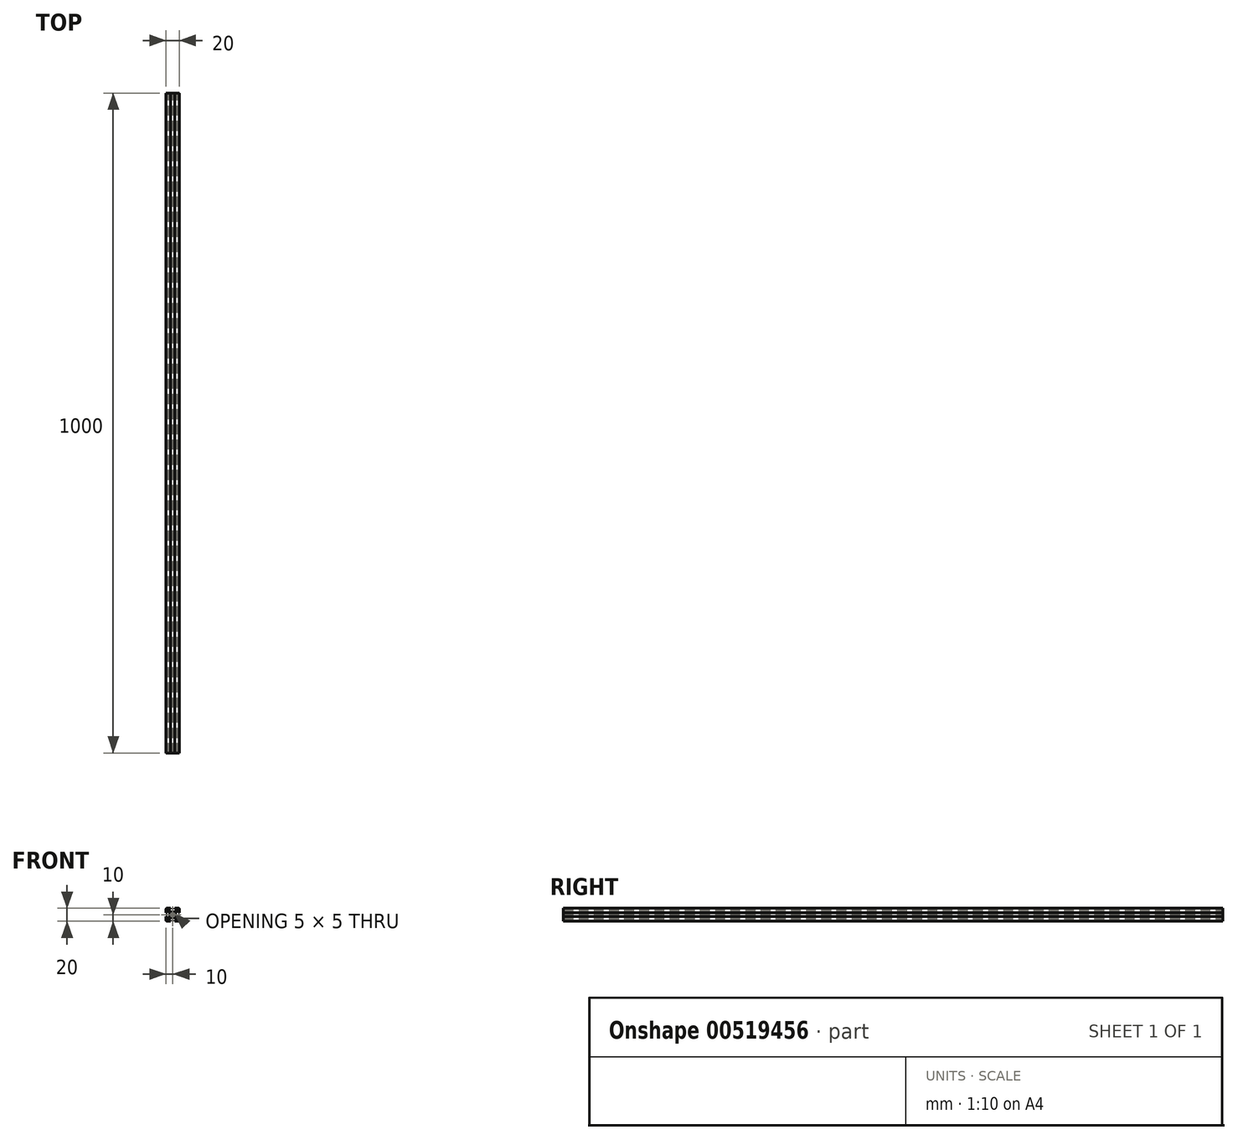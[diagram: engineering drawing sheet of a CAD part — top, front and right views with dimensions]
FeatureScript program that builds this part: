
annotation { "Feature Type Name" : "Feature", "Feature Type Description" : "" }
export const myFeature = defineFeature(function(context is Context, id is Id, definition is map)
    precondition{}
    {
        {
            var Q0;
            Q0=qCreatedBy(makeId("Front.planeOp"),FACE);
            var sketch = newSketch(context, id + "F0", { "sketchPlane" : qUnion([Q0])});
            skLineSegment(sketch, "E0.bottom", {"start": v(8.5, -10) * mm, "end": v(3, -10) * mm});
            skLineSegment(sketch, "E0.top", {"start": v(8.5, 10) * mm, "end": v(3, 10) * mm});
            skLineSegment(sketch, "E0.left", {"start": v(10, -8.5) * mm, "end": v(10, -3) * mm});
            skLineSegment(sketch, "E0.right", {"start": v(-10, -8.5) * mm, "end": v(-10, -3) * mm});
            skPoint(sketch, "E0.middle", {"position": v(0, 0) * mm});
            skLineSegment(sketch, "E1.bottom", {"start": v(6, -8.5) * mm, "end": v(3, -8.5) * mm});
            skLineSegment(sketch, "E1.top", {"start": v(6, 8.5) * mm, "end": v(3, 8.5) * mm});
            skLineSegment(sketch, "E1.left", {"start": v(8.5, -6) * mm, "end": v(8.5, -3) * mm});
            skLineSegment(sketch, "E1.right", {"start": v(-8.5, -6) * mm, "end": v(-8.5, -3) * mm});
            skLineSegment(sketch, "E2.bottom", {"start": v(3.44, -4.5) * mm, "end": v(-3.44, -4.5) * mm});
            skLineSegment(sketch, "E2.top", {"start": v(3.44, 4.5) * mm, "end": v(-3.44, 4.5) * mm});
            skLineSegment(sketch, "E2.left", {"start": v(4.5, -3.44) * mm, "end": v(4.5, 3.44) * mm});
            skLineSegment(sketch, "E2.right", {"start": v(-4.5, -3.44) * mm, "end": v(-4.5, 3.44) * mm});
            skLineSegment(sketch, "E3.bottom", {"start": v(8.5, -6) * mm, "end": v(7.06, -6) * mm});
            skLineSegment(sketch, "E3.top", {"start": v(8.5, 6) * mm, "end": v(7.06, 6) * mm});
            skLineSegment(sketch, "E4.left", {"start": v(6, -8.5) * mm, "end": v(6, -7.06) * mm});
            skLineSegment(sketch, "E4.right", {"start": v(-6, -8.5) * mm, "end": v(-6, -7.06) * mm});
            skPoint(sketch, "E5.orphan", {"position": v(-8.5, 8.5) * mm});
            skPoint(sketch, "E6.orphan", {"position": v(8.5, 8.5) * mm});
            skPoint(sketch, "E7.orphan", {"position": v(8.5, -8.5) * mm});
            skPoint(sketch, "E8.orphan", {"position": v(-8.5, -8.5) * mm});
            skLineSegment(sketch, "E9.trimOffspring", {"start": v(-6, 7.06) * mm, "end": v(-6, 8.5) * mm});
            skLineSegment(sketch, "E10.trimOffspring", {"start": v(-7.06, 6) * mm, "end": v(-8.5, 6) * mm});
            skLineSegment(sketch, "E11.trimOffspring", {"start": v(6, 7.06) * mm, "end": v(6, 8.5) * mm});
            skLineSegment(sketch, "E12.trimOffspring", {"start": v(-7.06, -6) * mm, "end": v(-8.5, -6) * mm});
            skLineSegment(sketch, "E13", {"start": v(-10, 10) * mm, "end": v(0, 0) * mm, "construction": true});
            skLineSegment(sketch, "E14", {"start": v(10, 10) * mm, "end": v(0, 0) * mm, "construction": true});
            skLineSegment(sketch, "E15", {"start": v(-6, 7.06) * mm, "end": v(-3.44, 4.5) * mm});
            skPoint(sketch, "E15.endSnap0", {"position": v(7.25, -6) * mm});
            skLineSegment(sketch, "E16", {"start": v(6, -7.06) * mm, "end": v(3.44, -4.5) * mm});
            skLineSegment(sketch, "E17", {"start": v(7.06, 6) * mm, "end": v(4.5, 3.44) * mm});
            skLineSegment(sketch, "E18", {"start": v(6, 7.06) * mm, "end": v(3.44, 4.5) * mm});
            skPoint(sketch, "E19.orphan", {"position": v(6, -6) * mm});
            skPoint(sketch, "E20.orphan", {"position": v(-4.5, -4.5) * mm});
            skPoint(sketch, "E21.orphan", {"position": v(-4.5, 4.5) * mm});
            skPoint(sketch, "E22.orphan", {"position": v(4.5, 4.5) * mm});
            skPoint(sketch, "E23.orphan", {"position": v(4.5, -4.5) * mm});
            skLineSegment(sketch, "E24.trimOffspring", {"start": v(4.5, -3.44) * mm, "end": v(7.06, -6) * mm});
            skLineSegment(sketch, "E25.trimOffspring", {"start": v(-3.44, -4.5) * mm, "end": v(-6, -7.06) * mm});
            skLineSegment(sketch, "E26.trimOffspring", {"start": v(-4.5, -3.44) * mm, "end": v(-7.06, -6) * mm});
            skLineSegment(sketch, "E27.trimOffspring", {"start": v(-4.5, 3.44) * mm, "end": v(-7.06, 6) * mm});
            skLineSegment(sketch, "E28.bottom", {"start": v(8.5, -3) * mm, "end": v(10, -3) * mm});
            skLineSegment(sketch, "E28.top", {"start": v(8.5, 3) * mm, "end": v(10, 3) * mm});
            skPoint(sketch, "E28.middle", {"position": v(10, 0) * mm});
            skLineSegment(sketch, "E29.left", {"start": v(3, 8.5) * mm, "end": v(3, 10) * mm});
            skLineSegment(sketch, "E29.right", {"start": v(-3, 8.5) * mm, "end": v(-3, 10) * mm});
            skPoint(sketch, "E29.middle", {"position": v(0, 10) * mm});
            skLineSegment(sketch, "E30.bottom", {"start": v(-8.5, 3) * mm, "end": v(-10, 3) * mm});
            skLineSegment(sketch, "E30.top", {"start": v(-8.5, -3) * mm, "end": v(-10, -3) * mm});
            skPoint(sketch, "E30.middle", {"position": v(-10, 0) * mm});
            skLineSegment(sketch, "E31.left", {"start": v(3, -8.5) * mm, "end": v(3, -10) * mm});
            skLineSegment(sketch, "E31.right", {"start": v(-3, -8.5) * mm, "end": v(-3, -10) * mm});
            skPoint(sketch, "E31.middle", {"position": v(0, -10) * mm});
            skPoint(sketch, "E32.orphan", {"position": v(3, 11.5) * mm});
            skPoint(sketch, "E33.orphan", {"position": v(-3, 11.5) * mm});
            skLineSegment(sketch, "E34.trimOffspring", {"start": v(-3, 10) * mm, "end": v(-8.5, 10) * mm});
            skLineSegment(sketch, "E35.trimOffspring", {"start": v(-3, 8.5) * mm, "end": v(-6, 8.5) * mm});
            skPoint(sketch, "E28.right.end.orphan", {"position": v(11.5, 3) * mm});
            skPoint(sketch, "E36.orphan", {"position": v(11.5, -3) * mm});
            skLineSegment(sketch, "E37.trimOffspring", {"start": v(10, 3) * mm, "end": v(10, 8.5) * mm});
            skLineSegment(sketch, "E38.trimOffspring", {"start": v(8.5, 3) * mm, "end": v(8.5, 6) * mm});
            skPoint(sketch, "E39.orphan", {"position": v(3, -11.5) * mm});
            skPoint(sketch, "E40.orphan", {"position": v(-3, -11.5) * mm});
            skLineSegment(sketch, "E41.trimOffspring", {"start": v(-3, -10) * mm, "end": v(-8.5, -10) * mm});
            skLineSegment(sketch, "E42.trimOffspring", {"start": v(-3, -8.5) * mm, "end": v(-6, -8.5) * mm});
            skPoint(sketch, "E30.right.end.orphan", {"position": v(-11.5, -3) * mm});
            skPoint(sketch, "E43.orphan", {"position": v(-11.5, 3) * mm});
            skLineSegment(sketch, "E44.trimOffspring", {"start": v(-10, 3) * mm, "end": v(-10, 8.5) * mm});
            skLineSegment(sketch, "E45.trimOffspring", {"start": v(-8.5, 3) * mm, "end": v(-8.5, 6) * mm});
            skLineSegment(sketch, "E46.trimOffspring", {"start": v(0, 0) * mm, "end": v(10, -10) * mm, "construction": true});
            skLineSegment(sketch, "E47.trimOffspring", {"start": v(0, 0) * mm, "end": v(-10, -10) * mm, "construction": true});
            skArc(sketch, "E48", {"start": v(1.16, 2.22) * mm, "mid": v(0, 2.5) * mm, "end": v(-1.16, 2.22) * mm});
            skLineSegment(sketch, "E49", {"start": v(-2.5, -1.44) * mm, "end": v(1.44, 2.5) * mm});
            skLineSegment(sketch, "E50", {"start": v(2.5, 1.44) * mm, "end": v(-1.44, -2.5) * mm});
            skLineSegment(sketch, "E51", {"start": v(1.44, -2.5) * mm, "end": v(-2.5, 1.44) * mm});
            skLineSegment(sketch, "E52", {"start": v(-1.44, 2.5) * mm, "end": v(2.5, -1.44) * mm});
            skLineSegment(sketch, "E53", {"start": v(2.5, 1.44) * mm, "end": v(2.5, -1.44) * mm, "construction": true});
            skLineSegment(sketch, "E54", {"start": v(1.44, -2.5) * mm, "end": v(-1.44, -2.5) * mm, "construction": true});
            skLineSegment(sketch, "E55", {"start": v(-2.5, -1.44) * mm, "end": v(-2.5, 1.44) * mm, "construction": true});
            skLineSegment(sketch, "E56", {"start": v(-1.44, 2.5) * mm, "end": v(1.44, 2.5) * mm, "construction": true});
            skLineSegment(sketch, "E57", {"start": v(-1.44, 2.5) * mm, "end": v(-2.5, 1.44) * mm});
            skLineSegment(sketch, "E58", {"start": v(1.44, 2.5) * mm, "end": v(2.5, 1.44) * mm});
            skLineSegment(sketch, "E59", {"start": v(2.5, -1.44) * mm, "end": v(1.44, -2.5) * mm});
            skLineSegment(sketch, "E60", {"start": v(-1.44, -2.5) * mm, "end": v(-2.5, -1.44) * mm});
            skArc(sketch, "E61.trimOffspring", {"start": v(-2.22, 1.16) * mm, "mid": v(-2.5, 0) * mm, "end": v(-2.22, -1.16) * mm});
            skArc(sketch, "E62.trimOffspring", {"start": v(-1.16, -2.22) * mm, "mid": v(0, -2.5) * mm, "end": v(1.16, -2.22) * mm});
            skArc(sketch, "E63.trimOffspring", {"start": v(2.22, -1.16) * mm, "mid": v(2.5, 0) * mm, "end": v(2.22, 1.16) * mm});
            skPoint(sketch, "E64.visualSharp", {"position": v(10, 10) * mm});
            skArc(sketch, "E64.filletArc", {"start": v(10, 8.5) * mm, "mid": v(9.56, 9.56) * mm, "end": v(8.5, 10) * mm});
            skPoint(sketch, "E65.visualSharp", {"position": v(10, -10) * mm});
            skArc(sketch, "E65.filletArc", {"start": v(8.5, -10) * mm, "mid": v(9.56, -9.56) * mm, "end": v(10, -8.5) * mm});
            skPoint(sketch, "E66.visualSharp", {"position": v(-10, -10) * mm});
            skArc(sketch, "E66.filletArc", {"start": v(-10, -8.5) * mm, "mid": v(-9.56, -9.56) * mm, "end": v(-8.5, -10) * mm});
            skPoint(sketch, "E67.visualSharp", {"position": v(-10, 10) * mm});
            skArc(sketch, "E67.filletArc", {"start": v(-8.5, 10) * mm, "mid": v(-9.56, 9.56) * mm, "end": v(-10, 8.5) * mm});
            skSolve(sketch);
        }
        {
            assignVariable(context, id + "F2", {"name" : "Length", "anyValue" : 1000});
        }
        {
            var Q0;
            Q0=qSketchRegion(id+"F0",true);
            extrude(context, id + "F1", {"entities" : qUnion([Q0]), "depth" : (getVariable(context, 'Length')) * mm});
        }
    });
